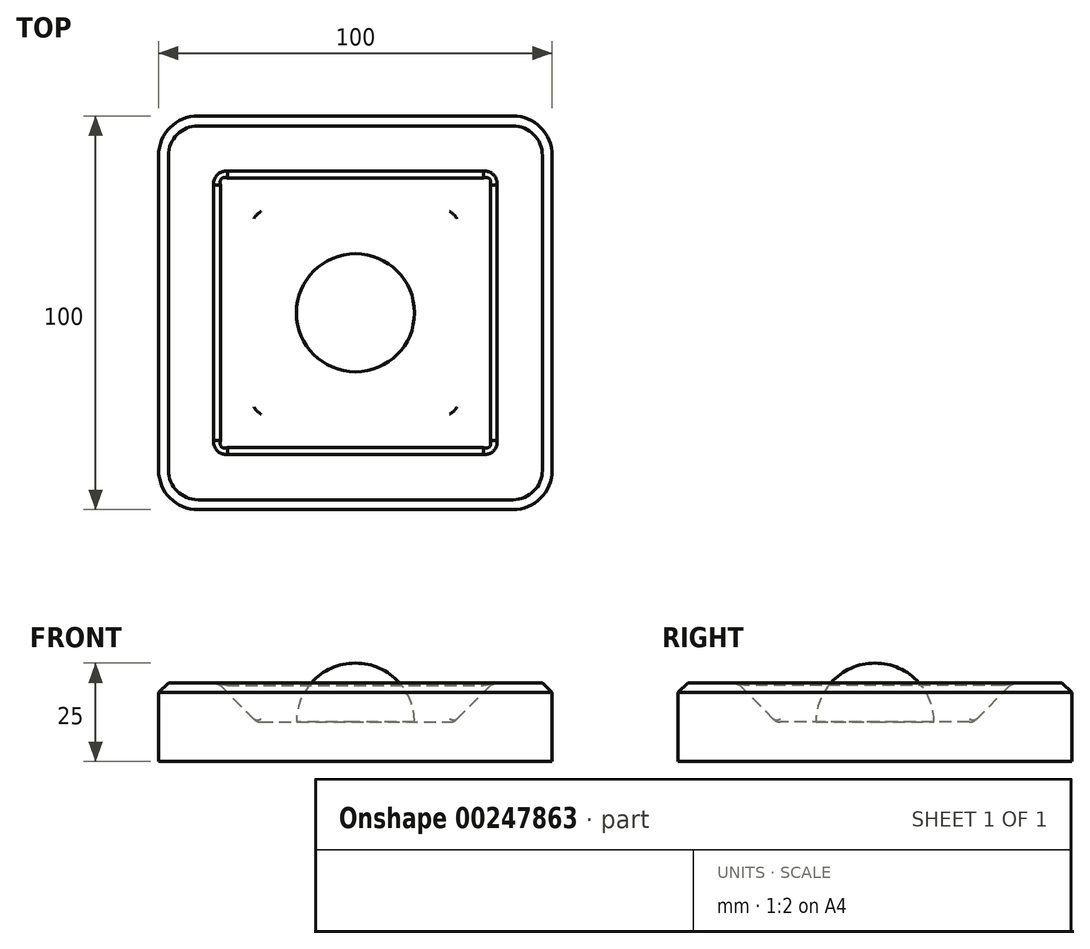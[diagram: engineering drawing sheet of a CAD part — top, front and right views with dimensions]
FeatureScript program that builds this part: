
annotation { "Feature Type Name" : "Feature", "Feature Type Description" : "" }
export const myFeature = defineFeature(function(context is Context, id is Id, definition is map)
    precondition{}
    {
        {
            var Q0;
            Q0=qCreatedBy(makeId("Top.planeOp"),FACE);
            var sketch = newSketch(context, id + "F0", { "sketchPlane" : qUnion([Q0])});
            skLineSegment(sketch, "E0.bottom", {"start": v(-50, 50) * mm, "end": v(50, 50) * mm});
            skLineSegment(sketch, "E0.top", {"start": v(-50, -50) * mm, "end": v(50, -50) * mm});
            skLineSegment(sketch, "E0.left", {"start": v(-50, 50) * mm, "end": v(-50, -50) * mm});
            skLineSegment(sketch, "E0.right", {"start": v(50, 50) * mm, "end": v(50, -50) * mm});
            skPoint(sketch, "E0.middle", {"position": v(0, 0) * mm});
            skSolve(sketch);
        }
        {
            var Q0;
            Q0=makeQuery(id+"F0.imprint","IMPRINT",FACE,{"disambiguationData":[TD([[makeQuery(id+"F0.imprint","IMPRINT",EDGE,{"derivedFrom":sQuery(id+"F0.wireOp",EDGE,"E0.bottom")}),-1.0]])]});
            extrude(context, id + "F1", {"entities" : qUnion([Q0]), "depth" : 20 * mm});
        }
        {
            var Q0;
            Q0=makeQuery(id+"F1.opExtrude","CAP_FACE",FACE,{"disambiguationData":[OSD([sQuery(id+"F0.wireOp",EDGE,"E0.bottom"),sQuery(id+"F0.wireOp",EDGE,"E0.top"),sQuery(id+"F0.wireOp",EDGE,"E0.left"),sQuery(id+"F0.wireOp",EDGE,"E0.right")])],"isStart":false});
            var sketch = newSketch(context, id + "F2", { "sketchPlane" : qUnion([Q0])});
            skLineSegment(sketch, "E1.0", {"start": v(-35, 35) * mm, "end": v(35, 35) * mm});
            skLineSegment(sketch, "E2.0", {"start": v(-35, 35) * mm, "end": v(-35, -35) * mm});
            skLineSegment(sketch, "E3.0", {"start": v(-55, 55) * mm, "end": v(-55, -55) * mm});
            skLineSegment(sketch, "E3.1", {"start": v(55, 55) * mm, "end": v(-55, 55) * mm});
            skLineSegment(sketch, "E3.2", {"start": v(55, -55) * mm, "end": v(55, 55) * mm});
            skLineSegment(sketch, "E3.3", {"start": v(-55, -55) * mm, "end": v(55, -55) * mm});
            skLineSegment(sketch, "E4.0", {"start": v(-35, -35) * mm, "end": v(35, -35) * mm});
            skLineSegment(sketch, "E5.0", {"start": v(35, 35) * mm, "end": v(35, -35) * mm});
            skSolve(sketch);
        }
        {
            var Q0;
            Q0=makeQuery(id+"F2.imprint","IMPRINT",FACE,{"disambiguationData":[TD([[makeQuery(id+"F2.imprint","IMPRINT",EDGE,{"derivedFrom":sQuery(id+"F2.wireOp",EDGE,"E1.0")}),-1.0]])]});
            extrude(context, id + "F3", {"entities" : qUnion([Q0]), "operationType" : NewBodyOperationType.REMOVE, "oppositeDirection" : true, "depth" : 10 * mm, "hasDraft" : true, "draftAngle" : 45 * degree, "draftPullDirection" : true});
        }
        {
            var Q0;
            Q0=makeQuery(id+"F3.boolean.opBoolean","COPY",FACE,{"derivedFrom":makeQuery(id+"F3.opExtrude","CAP_FACE",FACE,{"disambiguationData":[OSD([sQuery(id+"F2.wireOp",EDGE,"E1.0"),sQuery(id+"F2.wireOp",EDGE,"E2.0"),sQuery(id+"F2.wireOp",EDGE,"E4.0"),sQuery(id+"F2.wireOp",EDGE,"E5.0")])],"isStart":false})});
            var sketch = newSketch(context, id + "F4", { "sketchPlane" : qUnion([Q0])});
            skArc(sketch, "E6", {"start": v(0, -15) * mm, "mid": v(15, 0) * mm, "end": v(0, 15) * mm});
            skLineSegment(sketch, "E7", {"start": v(0, 15) * mm, "end": v(0, -15) * mm});
            skSolve(sketch);
        }
        {
            var Q0;
            Q0=makeQuery(id+"F4.imprint","IMPRINT",FACE,{"disambiguationData":[TD([[makeQuery(id+"F4.imprint","IMPRINT",EDGE,{"derivedFrom":sQuery(id+"F4.wireOp",EDGE,"E6")}),1.0]])]});
            var Q1;
            Q1=sQuery(id+"F4.wireOp",EDGE,"E7");
            revolve(context, id + "F5", {"operationType" : NewBodyOperationType.ADD, "entities" : qUnion([Q0]), "axis" : qUnion([Q1]), "revolveType" : RevolveType.FULL});
        }
        {
            var Q0;
            Q0=makeQuery(id+"F1.opExtrude","SWEPT_FACE",FACE,{"disambiguationData":[OSD([sQuery(id+"F0.wireOp",EDGE,"E0.top")])]});
            var sketch = newSketch(context, id + "F6", { "sketchPlane" : qUnion([Q0])});
            skLineSegment(sketch, "E8.0", {"start": v(-50, 0) * mm, "end": v(50, 0) * mm});
            skLineSegment(sketch, "E9", {"start": v(-50, 0) * mm, "end": v(-50, -10) * mm});
            skLineSegment(sketch, "E10", {"start": v(-50, -10) * mm, "end": v(50, -10) * mm});
            skLineSegment(sketch, "E11", {"start": v(50, 0) * mm, "end": v(50, -10) * mm});
            skSolve(sketch);
        }
        {
            var Q0;
            Q0 = qSketchRegion(id + "F6", true);
            extrude(context, id + "F7", {"entities" : qUnion([Q0]), "operationType" : NewBodyOperationType.REMOVE, "oppositeDirection" : true, "depth" : 116 * mm});
        }
        {
            var Q0;
            Q0=makeQuery(id+"F1.opExtrude","SWEPT_EDGE",EDGE,{"disambiguationData":[OSD([sQuery(id+"F0.wireOp",EDGE,"E0.top"),sQuery(id+"F0.wireOp",EDGE,"E0.right")])]});
            var Q1;
            Q1=makeQuery(id+"F1.opExtrude","SWEPT_EDGE",EDGE,{"disambiguationData":[OSD([sQuery(id+"F0.wireOp",EDGE,"E0.top"),sQuery(id+"F0.wireOp",EDGE,"E0.left")])]});
            var Q2;
            Q2=makeQuery(id+"F1.opExtrude","SWEPT_EDGE",EDGE,{"disambiguationData":[OSD([sQuery(id+"F0.wireOp",EDGE,"E0.bottom"),sQuery(id+"F0.wireOp",EDGE,"E0.left")])]});
            var Q3;
            Q3=makeQuery(id+"F1.opExtrude","SWEPT_EDGE",EDGE,{"disambiguationData":[OSD([sQuery(id+"F0.wireOp",EDGE,"E0.bottom"),sQuery(id+"F0.wireOp",EDGE,"E0.right")])]});
            fillet(context, id + "F8", {"entities" : qUnion([Q0, Q1, Q2, Q3]), "radius" : 10 * mm, "tangentPropagation" : true, "allowEdgeOverflow" : false});
        }
        {
            var Q0;
            Q0=makeQuery(id+"F3.boolean.opBoolean","COPY",EDGE,{"derivedFrom":makeQuery(id+"F3.opExtrude","CAP_EDGE",EDGE,{"disambiguationData":[OSD([sQuery(id+"F2.wireOp",EDGE,"E5.0")])],"isStart":true})});
            var Q1;
            Q1=makeQuery(id+"F3.boolean.opBoolean","COPY",EDGE,{"derivedFrom":makeQuery(id+"F3.opExtrude","CAP_EDGE",EDGE,{"disambiguationData":[OSD([sQuery(id+"F2.wireOp",EDGE,"E4.0")])],"isStart":true})});
            var Q2;
            Q2=makeQuery(id+"F3.boolean.opBoolean","COPY",EDGE,{"derivedFrom":makeQuery(id+"F3.opExtrude","CAP_EDGE",EDGE,{"disambiguationData":[OSD([sQuery(id+"F2.wireOp",EDGE,"E2.0")])],"isStart":true})});
            var Q3;
            Q3=makeQuery(id+"F3.boolean.opBoolean","COPY",EDGE,{"derivedFrom":makeQuery(id+"F3.opExtrude","CAP_EDGE",EDGE,{"disambiguationData":[OSD([sQuery(id+"F2.wireOp",EDGE,"E1.0")])],"isStart":true})});
            var Q4;
            Q4=makeQuery(id+"F3.boolean.opBoolean","COPY",EDGE,{"derivedFrom":makeQuery(id+"F3.opExtrude","SWEPT_EDGE",EDGE,{"disambiguationData":[OSD([sQuery(id+"F2.wireOp",EDGE,"E4.0"),sQuery(id+"F2.wireOp",EDGE,"E5.0")])]})});
            var Q5;
            Q5=makeQuery(id+"F3.boolean.opBoolean","COPY",EDGE,{"derivedFrom":makeQuery(id+"F3.opExtrude","SWEPT_EDGE",EDGE,{"disambiguationData":[OSD([sQuery(id+"F2.wireOp",EDGE,"E2.0"),sQuery(id+"F2.wireOp",EDGE,"E4.0")])]})});
            var Q6;
            Q6=makeQuery(id+"F3.boolean.opBoolean","COPY",EDGE,{"derivedFrom":makeQuery(id+"F3.opExtrude","SWEPT_EDGE",EDGE,{"disambiguationData":[OSD([sQuery(id+"F2.wireOp",EDGE,"E1.0"),sQuery(id+"F2.wireOp",EDGE,"E5.0")])]})});
            var Q7;
            Q7=makeQuery(id+"F3.boolean.opBoolean","COPY",EDGE,{"derivedFrom":makeQuery(id+"F3.opExtrude","SWEPT_EDGE",EDGE,{"disambiguationData":[OSD([sQuery(id+"F2.wireOp",EDGE,"E1.0"),sQuery(id+"F2.wireOp",EDGE,"E2.0")])]})});
            var Q8;
            Q8=makeQuery(id+"F3.boolean.opBoolean","COPY",EDGE,{"derivedFrom":makeQuery(id+"F3.opExtrude","CAP_EDGE",EDGE,{"disambiguationData":[OSD([sQuery(id+"F2.wireOp",EDGE,"E1.0")])],"isStart":false})});
            var Q9;
            Q9=makeQuery(id+"F3.boolean.opBoolean","COPY",EDGE,{"derivedFrom":makeQuery(id+"F3.opExtrude","CAP_EDGE",EDGE,{"disambiguationData":[OSD([sQuery(id+"F2.wireOp",EDGE,"E2.0")])],"isStart":false})});
            var Q10;
            Q10=makeQuery(id+"F3.boolean.opBoolean","COPY",EDGE,{"derivedFrom":makeQuery(id+"F3.opExtrude","CAP_EDGE",EDGE,{"disambiguationData":[OSD([sQuery(id+"F2.wireOp",EDGE,"E5.0")])],"isStart":false})});
            var Q11;
            Q11=makeQuery(id+"F3.boolean.opBoolean","COPY",EDGE,{"derivedFrom":makeQuery(id+"F3.opExtrude","CAP_EDGE",EDGE,{"disambiguationData":[OSD([sQuery(id+"F2.wireOp",EDGE,"E4.0")])],"isStart":false})});
            fillet(context, id + "F9", {"entities" : qUnion([Q0, Q1, Q2, Q3, Q4, Q5, Q6, Q7, Q8, Q9, Q10, Q11]), "radius" : 2.5 * mm, "tangentPropagation" : true, "allowEdgeOverflow" : false});
        }
        {
            var Q0;
            Q0=makeQuery(id+"F1.opExtrude","CAP_FACE",FACE,{"disambiguationData":[OSD([sQuery(id+"F0.wireOp",EDGE,"E0.bottom"),sQuery(id+"F0.wireOp",EDGE,"E0.top"),sQuery(id+"F0.wireOp",EDGE,"E0.left"),sQuery(id+"F0.wireOp",EDGE,"E0.right")])],"isStart":false});
            chamfer(context, id + "F10", {"entities" : qUnion([Q0]), "width" : 2.5 * mm, "tangentPropagation" : true});
        }
    });
